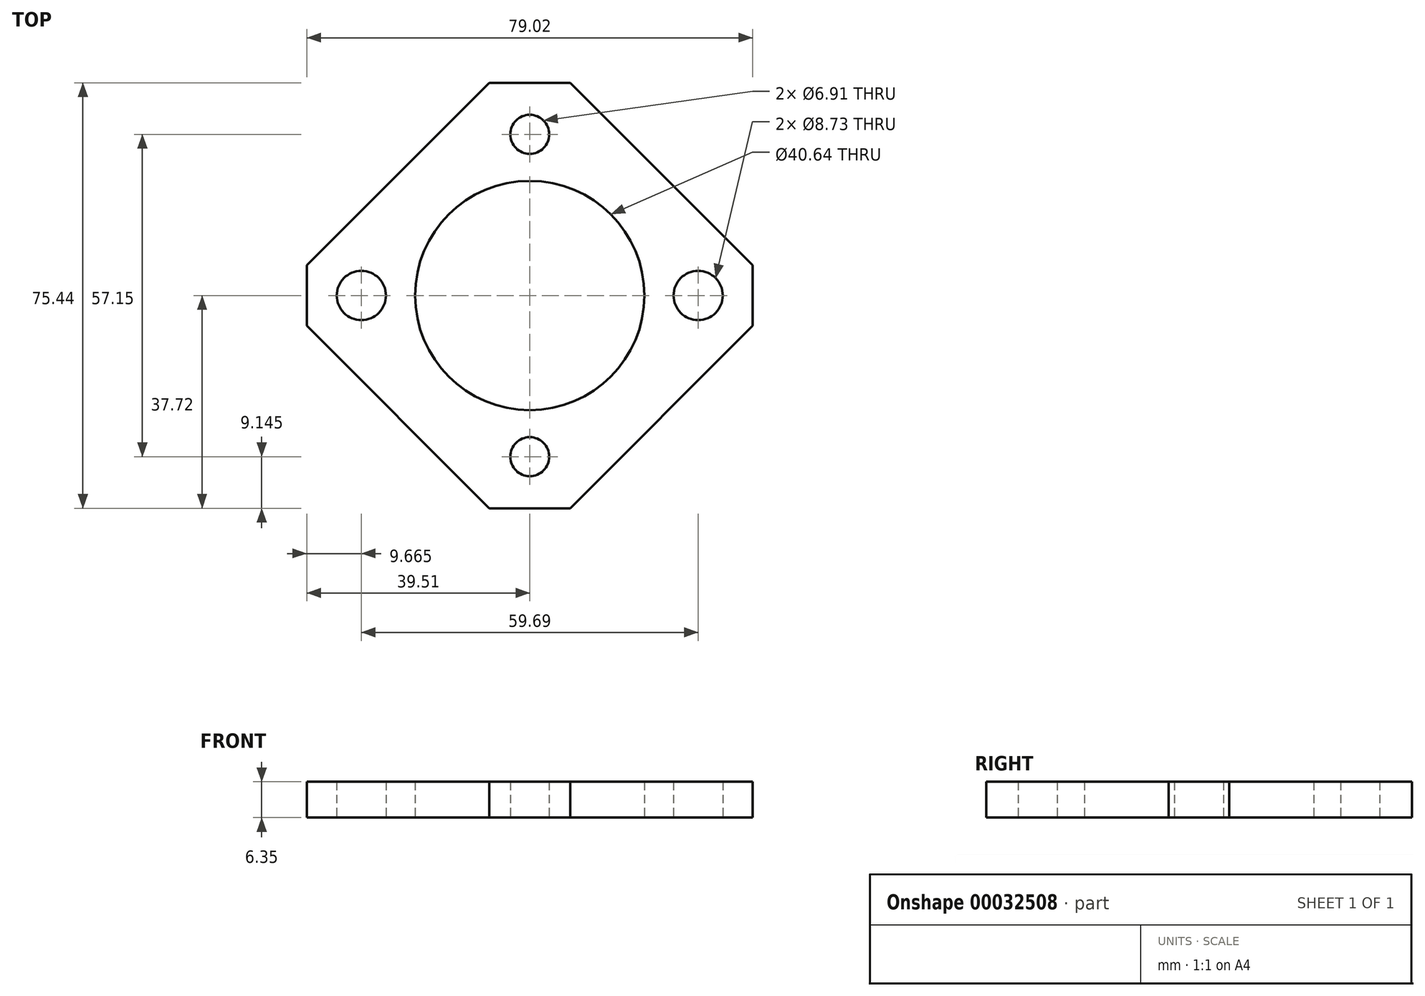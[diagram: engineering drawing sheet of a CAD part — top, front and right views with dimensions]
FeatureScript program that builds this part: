
annotation { "Feature Type Name" : "Feature", "Feature Type Description" : "" }
export const myFeature = defineFeature(function(context is Context, id is Id, definition is map)
    precondition{}
    {
        {
            var Q0;
            Q0=qCreatedBy(makeId("Top.planeOp"),FACE);
            var sketch = newSketch(context, id + "F0", { "sketchPlane" : qUnion([Q0])});
            skLineSegment(sketch, "E0", {"start": v(0, 44.9) * mm, "end": v(-44.9, 0) * mm});
            skLineSegment(sketch, "E1", {"start": v(-44.9, 0) * mm, "end": v(0, -44.9) * mm});
            skLineSegment(sketch, "E2", {"start": v(0, -44.9) * mm, "end": v(44.9, 0) * mm});
            skLineSegment(sketch, "E3", {"start": v(44.9, 0) * mm, "end": v(0, 44.9) * mm});
            skCircle(sketch, "E4", {"center": v(0, 0) * mm, "radius": 20.32 * mm});
            skCircle(sketch, "E5", {"center": v(0, 28.58) * mm, "radius": 3.45 * mm});
            skCircle(sketch, "E6", {"center": v(0, -28.58) * mm, "radius": 3.45 * mm});
            skCircle(sketch, "E7", {"center": v(-29.85, 0) * mm, "radius": 4.37 * mm});
            skCircle(sketch, "E8", {"center": v(29.85, 0) * mm, "radius": 4.37 * mm});
            skLineSegment(sketch, "E9", {"start": v(0, 28.58) * mm, "end": v(0, -28.58) * mm, "construction": true});
            skLineSegment(sketch, "E10", {"start": v(-29.85, 0) * mm, "end": v(29.85, 0) * mm, "construction": true});
            skSolve(sketch);
        }
        {
            var Q0;
            Q0 = qSketchRegion(id + "F0", true);
            extrude(context, id + "F1", {"entities" : qUnion([Q0]), "depth" : 6.35 * mm});
        }
        {
            var Q0;
            Q0=makeQuery(id+"F1.opExtrude","SWEPT_EDGE",EDGE,{"disambiguationData":[OSD([sQuery(id+"F0.wireOp",EDGE,"E0"),sQuery(id+"F0.wireOp",EDGE,"E3")])]});
            var Q1;
            Q1=makeQuery(id+"F1.opExtrude","SWEPT_EDGE",EDGE,{"disambiguationData":[OSD([sQuery(id+"F0.wireOp",EDGE,"E1"),sQuery(id+"F0.wireOp",EDGE,"E2")])]});
            chamfer(context, id + "F2", {"entities" : qUnion([Q0, Q1]), "width" : 10.16 * mm, "tangentPropagation" : true});
        }
        {
            var Q0;
            Q0=makeQuery(id+"F1.opExtrude","SWEPT_EDGE",EDGE,{"disambiguationData":[OSD([sQuery(id+"F0.wireOp",EDGE,"E0"),sQuery(id+"F0.wireOp",EDGE,"E1")])]});
            var Q1;
            Q1=makeQuery(id+"F1.opExtrude","SWEPT_EDGE",EDGE,{"disambiguationData":[OSD([sQuery(id+"F0.wireOp",EDGE,"E2"),sQuery(id+"F0.wireOp",EDGE,"E3")])]});
            chamfer(context, id + "F3", {"entities" : qUnion([Q0, Q1]), "width" : 7.62 * mm, "tangentPropagation" : true});
        }
    });
